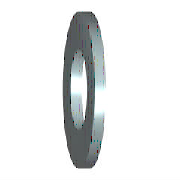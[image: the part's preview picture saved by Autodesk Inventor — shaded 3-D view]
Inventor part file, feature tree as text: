
AUTODESK INVENTOR PART (.ipt)
format: ipt  version: 2022 (Build 260153000, 153)  size: 107,520 bytes
history: native  units: mm (DEFAULTED — no unit token found)
features: other x1, plane x1, sketch x1
ambient origin geometry x7: Origin, YZ Plane, XY Plane, X Axis, Y Axis, Z Axis, Center Point
bodies: Solid1 (feature_tree), Body (feature_tree)
feature tree (3):
  other  "Work Axis1"
  plane  "Work Plane1"
  sketch  "Sketch"  dims[d0=4.3mm d1=9.0mm d2=0.8mm d3=0.0mm d4=0.0mm d5=0.0mm d6=0.0mm d7=0.0mm]
